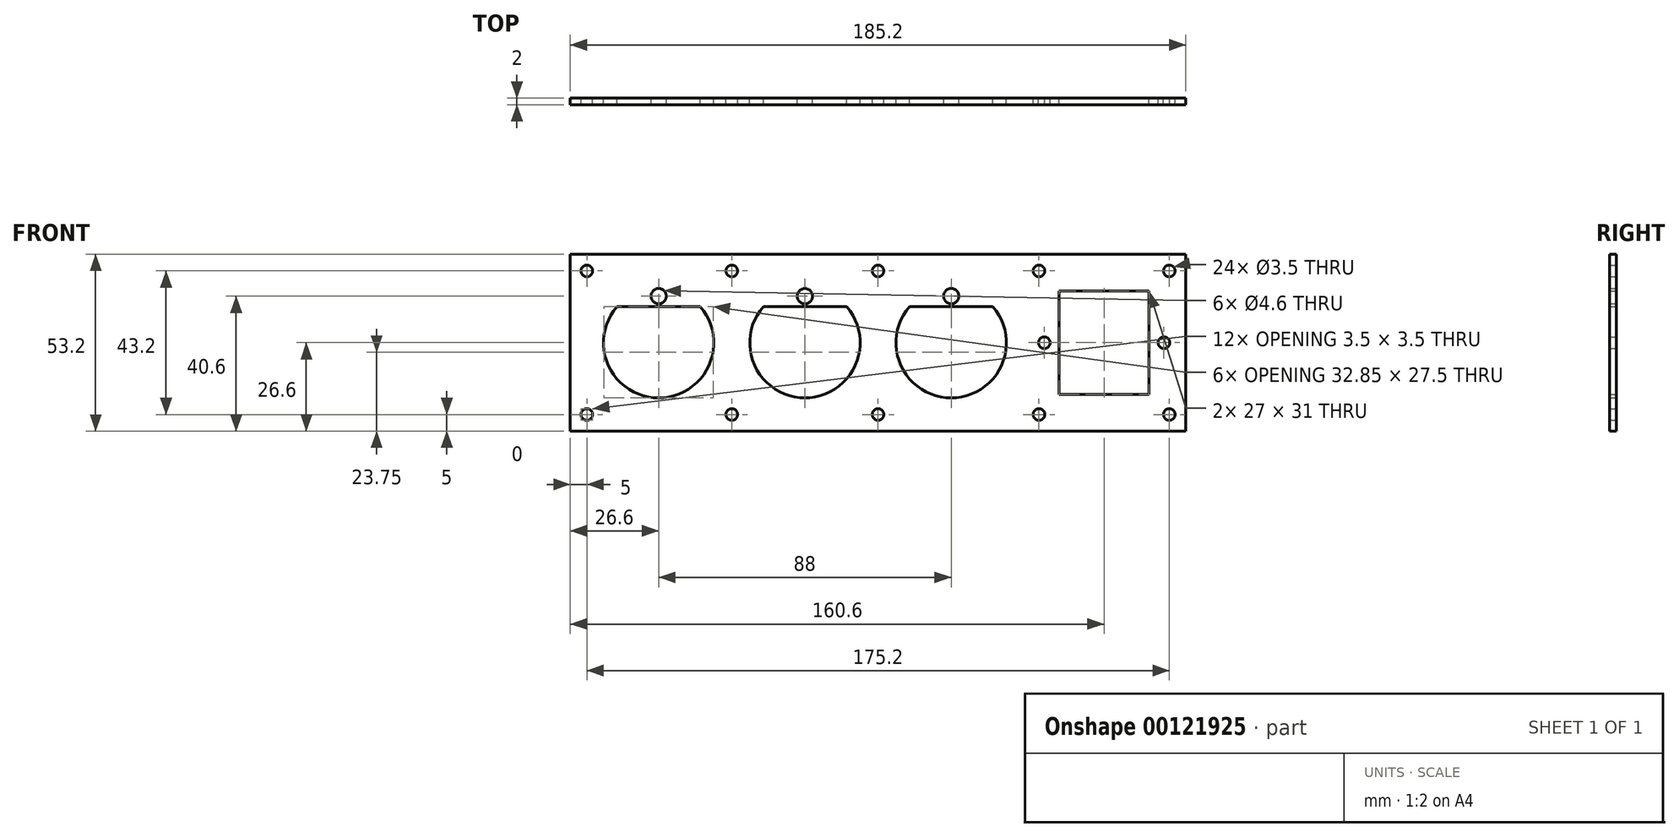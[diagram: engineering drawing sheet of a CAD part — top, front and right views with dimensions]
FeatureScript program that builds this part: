
annotation { "Feature Type Name" : "Feature", "Feature Type Description" : "" }
export const myFeature = defineFeature(function(context is Context, id is Id, definition is map)
    precondition{}
    {
        {
            var Q0;
            Q0=qCreatedBy(makeId("Front.planeOp"),FACE);
            var sketch = newSketch(context, id + "F0", { "sketchPlane" : qUnion([Q0])});
            skLineSegment(sketch, "E0", {"start": v(-52.65, 10.9) * mm, "end": v(15.7, 10.9) * mm, "construction": true});
            skLineSegment(sketch, "E1", {"start": v(-17.47, 14) * mm, "end": v(17.83, 14) * mm, "construction": true});
            skArc(sketch, "E2", {"start": v(-12.52, 10.9) * mm, "mid": v(0, -16.6) * mm, "end": v(12.52, 10.9) * mm});
            skCircle(sketch, "E3", {"center": v(0, 14) * mm, "radius": 2.3 * mm});
            skLineSegment(sketch, "E4", {"start": v(-12.52, 10.9) * mm, "end": v(12.52, 10.9) * mm});
            skCircle(sketch, "E5.1.0.0", {"center": v(44, 14) * mm, "radius": 2.3 * mm});
            skArc(sketch, "E5.1.0.1", {"start": v(31.48, 10.9) * mm, "mid": v(44, -16.6) * mm, "end": v(56.52, 10.9) * mm});
            skLineSegment(sketch, "E5.1.0.2", {"start": v(26.53, 14) * mm, "end": v(61.83, 14) * mm, "construction": true});
            skLineSegment(sketch, "E5.1.0.3", {"start": v(-8.65, 10.9) * mm, "end": v(59.7, 10.9) * mm, "construction": true});
            skLineSegment(sketch, "E5.1.0.4", {"start": v(31.48, 10.9) * mm, "end": v(56.52, 10.9) * mm});
            skCircle(sketch, "E5.2.0.0", {"center": v(88, 14) * mm, "radius": 2.3 * mm});
            skArc(sketch, "E5.2.0.1", {"start": v(75.48, 10.9) * mm, "mid": v(88, -16.6) * mm, "end": v(100.52, 10.9) * mm});
            skLineSegment(sketch, "E5.2.0.2", {"start": v(70.53, 14) * mm, "end": v(105.83, 14) * mm, "construction": true});
            skLineSegment(sketch, "E5.2.0.3", {"start": v(35.35, 10.9) * mm, "end": v(103.7, 10.9) * mm, "construction": true});
            skLineSegment(sketch, "E5.2.0.4", {"start": v(75.48, 10.9) * mm, "end": v(100.52, 10.9) * mm});
            skLineSegment(sketch, "E5.direction1", {"start": v(-52.65, 10.9) * mm, "end": v(-8.65, 10.9) * mm, "construction": true});
            skLineSegment(sketch, "E6.bottom", {"start": v(158.6, 26.6) * mm, "end": v(-26.6, 26.6) * mm});
            skLineSegment(sketch, "E6.top", {"start": v(158.6, -26.6) * mm, "end": v(-26.6, -26.6) * mm});
            skLineSegment(sketch, "E6.left", {"start": v(158.6, 26.6) * mm, "end": v(158.6, -26.6) * mm});
            skLineSegment(sketch, "E6.right", {"start": v(-26.6, 26.6) * mm, "end": v(-26.6, -26.6) * mm});
            skLineSegment(sketch, "E7.bottom", {"start": v(-21.6, 21.6) * mm, "end": v(153.6, 21.6) * mm, "construction": true});
            skLineSegment(sketch, "E7.top", {"start": v(-21.6, -21.6) * mm, "end": v(153.6, -21.6) * mm, "construction": true});
            skLineSegment(sketch, "E7.left", {"start": v(-21.6, 21.6) * mm, "end": v(-21.6, -21.6) * mm, "construction": true});
            skLineSegment(sketch, "E7.right", {"start": v(153.6, 21.6) * mm, "end": v(153.6, -21.6) * mm, "construction": true});
            skPoint(sketch, "E8", {"position": v(-21.6, 21.6) * mm});
            skPoint(sketch, "E9", {"position": v(153.6, 21.6) * mm});
            skPoint(sketch, "E10", {"position": v(153.6, -21.6) * mm});
            skPoint(sketch, "E11", {"position": v(-21.6, -21.6) * mm});
            skLineSegment(sketch, "E12", {"start": v(16.6, 0) * mm, "end": v(27.4, 0) * mm, "construction": true});
            skLineSegment(sketch, "E13", {"start": v(60.6, 0) * mm, "end": v(71.4, 0) * mm, "construction": true});
            skLineSegment(sketch, "E14", {"start": v(22, -21.6) * mm, "end": v(22, 21.6) * mm, "construction": true});
            skPoint(sketch, "E14.startSnap0", {"position": v(22, 0) * mm});
            skLineSegment(sketch, "E15", {"start": v(66, -21.6) * mm, "end": v(66, 21.6) * mm, "construction": true});
            skLineSegment(sketch, "E16", {"start": v(114.4, -21.6) * mm, "end": v(114.4, 21.6) * mm, "construction": true});
            skPoint(sketch, "E16.startSnap0", {"position": v(114.4, 0) * mm});
            skPoint(sketch, "E17", {"position": v(22, 21.6) * mm});
            skPoint(sketch, "E18", {"position": v(66, 21.6) * mm});
            skPoint(sketch, "E19", {"position": v(114.4, 21.6) * mm});
            skPoint(sketch, "E20", {"position": v(114.4, -21.6) * mm});
            skPoint(sketch, "E21", {"position": v(66, -21.6) * mm});
            skPoint(sketch, "E22", {"position": v(22, -21.6) * mm});
            skLineSegment(sketch, "E23", {"start": v(114.4, 0) * mm, "end": v(153.6, 0) * mm, "construction": true});
            skLineSegment(sketch, "E24", {"start": v(134, 0) * mm, "end": v(134, 16.27) * mm, "construction": true});
            skLineSegment(sketch, "E25", {"start": v(134, 0) * mm, "end": v(134, -16.6) * mm, "construction": true});
            skPoint(sketch, "E25.endSnap0", {"position": v(88, -16.6) * mm});
            skLineSegment(sketch, "E26.bottom", {"start": v(147.5, 15.5) * mm, "end": v(120.5, 15.5) * mm});
            skLineSegment(sketch, "E26.top", {"start": v(147.5, -15.5) * mm, "end": v(120.5, -15.5) * mm});
            skLineSegment(sketch, "E26.left", {"start": v(147.5, 15.5) * mm, "end": v(147.5, -15.5) * mm});
            skLineSegment(sketch, "E26.right", {"start": v(120.5, 15.5) * mm, "end": v(120.5, -15.5) * mm});
            skPoint(sketch, "E26.middle", {"position": v(134, 0) * mm});
            skPoint(sketch, "E27", {"position": v(116, 0) * mm});
            skPoint(sketch, "E28", {"position": v(152, 0) * mm});
            skPoint(sketch, "E28.positionSnap0", {"position": v(158.6, 0) * mm});
            skLineSegment(sketch, "E29.bottom", {"start": v(156, -16.5) * mm, "end": v(112, -16.5) * mm, "construction": true});
            skLineSegment(sketch, "E29.top", {"start": v(156, 16.5) * mm, "end": v(112, 16.5) * mm, "construction": true});
            skLineSegment(sketch, "E29.left", {"start": v(156, -16.5) * mm, "end": v(156, 16.5) * mm, "construction": true});
            skLineSegment(sketch, "E29.right", {"start": v(112, -16.5) * mm, "end": v(112, 16.5) * mm, "construction": true});
            skSolve(sketch);
        }
        {
            var Q0;
            Q0=makeQuery(id+"F0.imprint","IMPRINT",FACE,{"disambiguationData":[TD([[makeQuery(id+"F0.imprint","IMPRINT",EDGE,{"derivedFrom":sQuery(id+"F0.wireOp",EDGE,"E2")}),-1.0]])]});
            extrude(context, id + "F1", {"entities" : qUnion([Q0]), "depth" : 2 * mm});
        }
        {
            var Q0;
            Q0=sQuery(id+"F0.wireOp",VERTEX,"E8");
            var Q1;
            Q1=sQuery(id+"F0.wireOp",VERTEX,"E11");
            var Q2;
            Q2=sQuery(id+"F0.wireOp",VERTEX,"E9");
            var Q3;
            Q3=sQuery(id+"F0.wireOp",VERTEX,"E10");
            var Q4;
            Q4=sQuery(id+"F0.wireOp",VERTEX,"E17");
            var Q5;
            Q5=sQuery(id+"F0.wireOp",VERTEX,"E18");
            var Q6;
            Q6=sQuery(id+"F0.wireOp",VERTEX,"E19");
            var Q7;
            Q7=sQuery(id+"F0.wireOp",VERTEX,"E20");
            var Q8;
            Q8=sQuery(id+"F0.wireOp",VERTEX,"E21");
            var Q9;
            Q9=sQuery(id+"F0.wireOp",VERTEX,"E22");
            var Q10;
            Q10=sQuery(id+"F0.wireOp",VERTEX,"E27");
            var Q11;
            Q11=sQuery(id+"F0.wireOp",VERTEX,"E28");
            var Q12;
            Q12=makeQuery(id+"F1.opExtrude","SWEPT_BODY",BODY,{"disambiguationData":[OSD([sQuery(id+"F0.wireOp",EDGE,"E2"),sQuery(id+"F0.wireOp",EDGE,"E3"),sQuery(id+"F0.wireOp",EDGE,"E4"),sQuery(id+"F0.wireOp",EDGE,"E5.1.0.0"),sQuery(id+"F0.wireOp",EDGE,"E5.1.0.1"),sQuery(id+"F0.wireOp",EDGE,"E5.1.0.4"),sQuery(id+"F0.wireOp",EDGE,"E5.2.0.0"),sQuery(id+"F0.wireOp",EDGE,"E5.2.0.1"),sQuery(id+"F0.wireOp",EDGE,"E5.2.0.4"),sQuery(id+"F0.wireOp",EDGE,"E5.3.0.0"),sQuery(id+"F0.wireOp",EDGE,"E5.3.0.1"),sQuery(id+"F0.wireOp",EDGE,"E5.3.0.4"),sQuery(id+"F0.wireOp",EDGE,"E6.bottom"),sQuery(id+"F0.wireOp",EDGE,"E6.top"),sQuery(id+"F0.wireOp",EDGE,"E6.left"),sQuery(id+"F0.wireOp",EDGE,"E6.right")])]});
            hole(context, id + "F2", {"style" : HoleStyle.SIMPLE, "endStyle" : HoleEndStyle.THROUGH, "oppositeDirection" : true, "holeDiameter" : 3.5 * mm, "locations" : qUnion([Q0, Q1, Q2, Q3, Q4, Q5, Q6, Q7, Q8, Q9, Q10, Q11]), "scope" : qUnion([Q12]), "isTappedThrough" : true});
        }
    });
